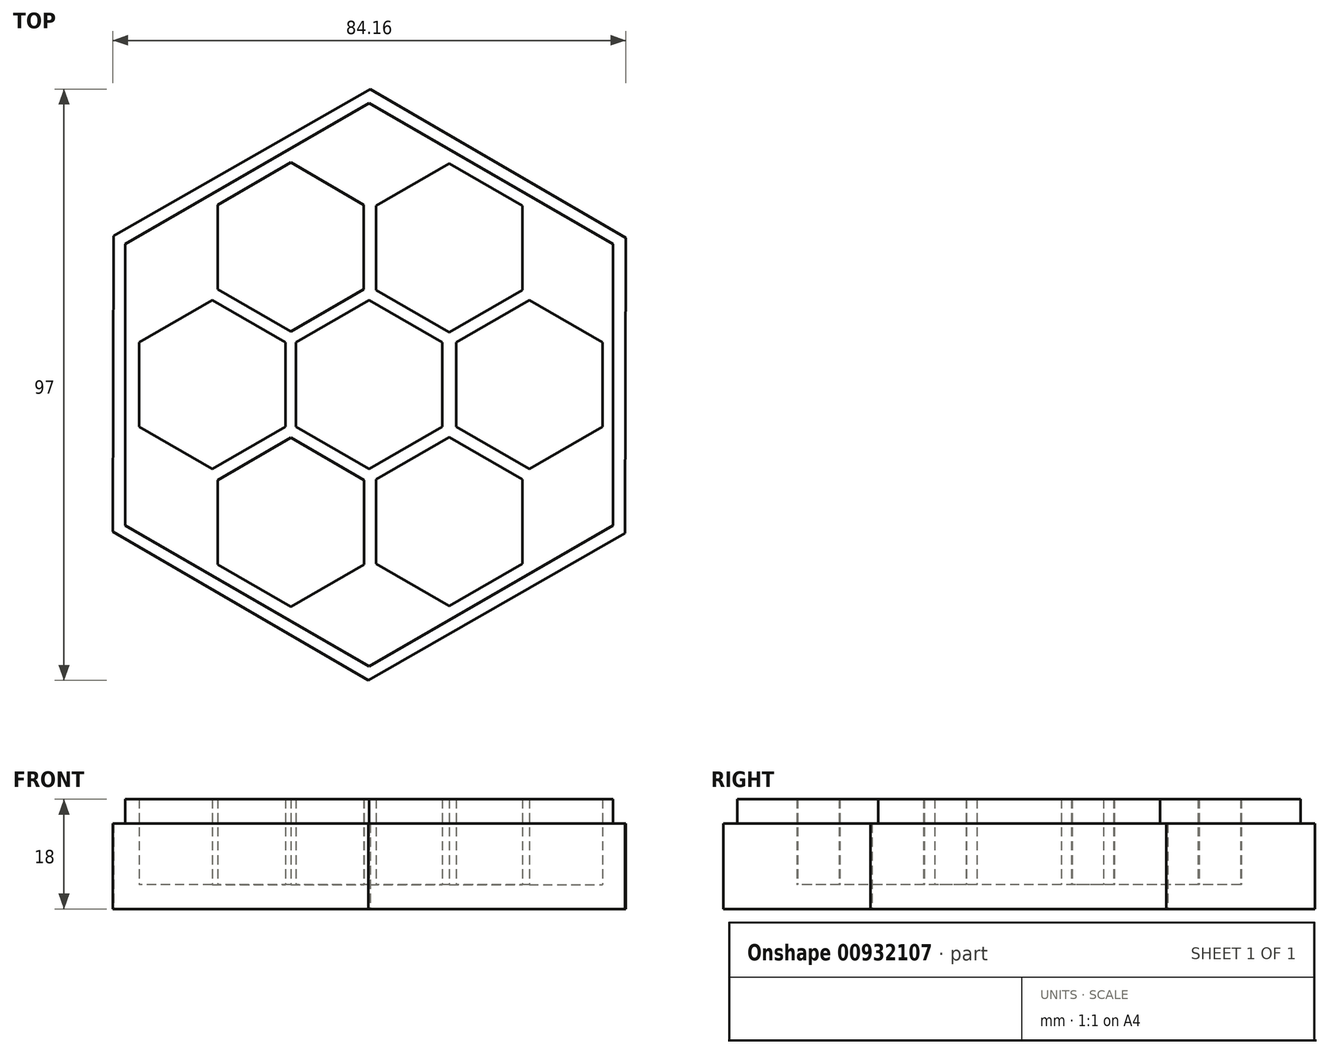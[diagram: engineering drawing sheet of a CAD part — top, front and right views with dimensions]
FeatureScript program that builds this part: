
annotation { "Feature Type Name" : "Feature", "Feature Type Description" : "" }
export const myFeature = defineFeature(function(context is Context, id is Id, definition is map)
    precondition{}
    {
        {
            var Q0;
            Q0=qCreatedBy(makeId("Top.planeOp"),FACE);
            var sketch = newSketch(context, id + "F0", { "sketchPlane" : qUnion([Q0])});
            skCircle(sketch, "E0.cCircle", {"center": v(0, 0) * mm, "radius": 12 * mm, "construction": true});
            skLineSegment(sketch, "E0.0", {"start": v(12, 6.93) * mm, "end": v(12, -6.93) * mm});
            skLineSegment(sketch, "E0.1", {"start": v(12, -6.93) * mm, "end": v(0, -13.86) * mm});
            skLineSegment(sketch, "E0.2", {"start": v(0, -13.86) * mm, "end": v(-12, -6.93) * mm});
            skLineSegment(sketch, "E0.3", {"start": v(-12, -6.93) * mm, "end": v(-12, 6.93) * mm});
            skLineSegment(sketch, "E0.4", {"start": v(-12, 6.93) * mm, "end": v(0, 13.86) * mm});
            skLineSegment(sketch, "E0.5", {"start": v(0, 13.86) * mm, "end": v(12, 6.93) * mm});
            skPoint(sketch, "E0.0.midPoint", {"position": v(12, 0) * mm});
            skCircle(sketch, "E1.cCircle", {"center": v(13.12, 22.45) * mm, "radius": 12 * mm, "construction": true});
            skLineSegment(sketch, "E1.0", {"start": v(25.12, 29.38) * mm, "end": v(25.12, 15.52) * mm});
            skLineSegment(sketch, "E1.1", {"start": v(25.12, 15.52) * mm, "end": v(13.12, 8.6) * mm});
            skLineSegment(sketch, "E1.2", {"start": v(13.12, 8.6) * mm, "end": v(1.12, 15.52) * mm});
            skLineSegment(sketch, "E1.3", {"start": v(1.12, 15.52) * mm, "end": v(1.12, 29.38) * mm});
            skLineSegment(sketch, "E1.4", {"start": v(1.12, 29.38) * mm, "end": v(13.12, 36.3) * mm});
            skLineSegment(sketch, "E1.5", {"start": v(13.12, 36.3) * mm, "end": v(25.12, 29.38) * mm});
            skPoint(sketch, "E1.0.midPoint", {"position": v(25.12, 22.45) * mm});
            skCircle(sketch, "E2.cCircle", {"center": v(-12.88, 22.58) * mm, "radius": 12 * mm, "construction": true});
            skLineSegment(sketch, "E2.0", {"start": v(-0.88, 29.51) * mm, "end": v(-0.88, 15.66) * mm});
            skLineSegment(sketch, "E2.1", {"start": v(-0.88, 15.66) * mm, "end": v(-12.88, 8.73) * mm});
            skLineSegment(sketch, "E2.2", {"start": v(-12.88, 8.73) * mm, "end": v(-24.88, 15.66) * mm});
            skLineSegment(sketch, "E2.3", {"start": v(-24.88, 15.66) * mm, "end": v(-24.88, 29.51) * mm});
            skLineSegment(sketch, "E2.4", {"start": v(-24.88, 29.51) * mm, "end": v(-12.88, 36.44) * mm});
            skLineSegment(sketch, "E2.5", {"start": v(-12.88, 36.44) * mm, "end": v(-0.88, 29.51) * mm});
            skPoint(sketch, "E2.0.midPoint", {"position": v(-0.88, 22.58) * mm});
            skCircle(sketch, "E3.cCircle", {"center": v(-25.77, 0) * mm, "radius": 12 * mm, "construction": true});
            skLineSegment(sketch, "E3.0", {"start": v(-13.77, 6.93) * mm, "end": v(-13.77, -6.93) * mm});
            skLineSegment(sketch, "E3.1", {"start": v(-13.77, -6.93) * mm, "end": v(-25.77, -13.86) * mm});
            skLineSegment(sketch, "E3.2", {"start": v(-25.77, -13.86) * mm, "end": v(-37.77, -6.93) * mm});
            skLineSegment(sketch, "E3.3", {"start": v(-37.77, -6.93) * mm, "end": v(-37.77, 6.93) * mm});
            skLineSegment(sketch, "E3.4", {"start": v(-37.77, 6.93) * mm, "end": v(-25.77, 13.86) * mm});
            skLineSegment(sketch, "E3.5", {"start": v(-25.77, 13.86) * mm, "end": v(-13.77, 6.93) * mm});
            skPoint(sketch, "E3.0.midPoint", {"position": v(-13.77, 0) * mm});
            skCircle(sketch, "E4.cCircle", {"center": v(13.14, -22.46) * mm, "radius": 12 * mm, "construction": true});
            skLineSegment(sketch, "E4.0", {"start": v(25.14, -15.54) * mm, "end": v(25.14, -29.4) * mm});
            skLineSegment(sketch, "E4.1", {"start": v(25.14, -29.4) * mm, "end": v(13.14, -36.32) * mm});
            skLineSegment(sketch, "E4.2", {"start": v(13.14, -36.32) * mm, "end": v(1.14, -29.4) * mm});
            skLineSegment(sketch, "E4.3", {"start": v(1.14, -29.4) * mm, "end": v(1.14, -15.54) * mm});
            skLineSegment(sketch, "E4.4", {"start": v(1.14, -15.54) * mm, "end": v(13.14, -8.6) * mm});
            skLineSegment(sketch, "E4.5", {"start": v(13.14, -8.6) * mm, "end": v(25.14, -15.54) * mm});
            skPoint(sketch, "E4.0.midPoint", {"position": v(25.14, -22.46) * mm});
            skCircle(sketch, "E5.cCircle", {"center": v(26.23, 0) * mm, "radius": 12 * mm, "construction": true});
            skLineSegment(sketch, "E5.0", {"start": v(38.23, 6.93) * mm, "end": v(38.23, -6.93) * mm});
            skLineSegment(sketch, "E5.1", {"start": v(38.23, -6.93) * mm, "end": v(26.23, -13.86) * mm});
            skLineSegment(sketch, "E5.2", {"start": v(26.23, -13.86) * mm, "end": v(14.23, -6.93) * mm});
            skLineSegment(sketch, "E5.3", {"start": v(14.23, -6.93) * mm, "end": v(14.23, 6.93) * mm});
            skLineSegment(sketch, "E5.4", {"start": v(14.23, 6.93) * mm, "end": v(26.23, 13.86) * mm});
            skLineSegment(sketch, "E5.5", {"start": v(26.23, 13.86) * mm, "end": v(38.23, 6.93) * mm});
            skPoint(sketch, "E5.0.midPoint", {"position": v(38.23, 0) * mm});
            skCircle(sketch, "E6.cCircle", {"center": v(-12.86, -22.57) * mm, "radius": 12 * mm, "construction": true});
            skLineSegment(sketch, "E6.0", {"start": v(-0.86, -15.64) * mm, "end": v(-0.86, -29.5) * mm});
            skLineSegment(sketch, "E6.1", {"start": v(-0.86, -29.5) * mm, "end": v(-12.86, -36.43) * mm});
            skLineSegment(sketch, "E6.2", {"start": v(-12.86, -36.43) * mm, "end": v(-24.86, -29.5) * mm});
            skLineSegment(sketch, "E6.3", {"start": v(-24.86, -29.5) * mm, "end": v(-24.86, -15.64) * mm});
            skLineSegment(sketch, "E6.4", {"start": v(-24.86, -15.64) * mm, "end": v(-12.86, -8.71) * mm});
            skLineSegment(sketch, "E6.5", {"start": v(-12.86, -8.71) * mm, "end": v(-0.86, -15.64) * mm});
            skPoint(sketch, "E6.0.midPoint", {"position": v(-0.86, -22.57) * mm});
            skCircle(sketch, "E7.cCircle", {"center": v(0, 0) * mm, "radius": 42 * mm, "construction": true});
            skLineSegment(sketch, "E7.0", {"start": v(0.16, 48.5) * mm, "end": v(42.08, 24.11) * mm});
            skLineSegment(sketch, "E7.1", {"start": v(42.08, 24.11) * mm, "end": v(41.92, -24.38) * mm});
            skLineSegment(sketch, "E7.2", {"start": v(41.92, -24.38) * mm, "end": v(-0.16, -48.5) * mm});
            skLineSegment(sketch, "E7.3", {"start": v(-0.16, -48.5) * mm, "end": v(-42.08, -24.11) * mm});
            skLineSegment(sketch, "E7.4", {"start": v(-42.08, -24.11) * mm, "end": v(-41.92, 24.38) * mm});
            skLineSegment(sketch, "E7.5", {"start": v(-41.92, 24.38) * mm, "end": v(0.16, 48.5) * mm});
            skPoint(sketch, "E7.0.midPoint", {"position": v(21.12, 36.3) * mm});
            skCircle(sketch, "E8.cCircle", {"center": v(0, 0) * mm, "radius": 40 * mm, "construction": true});
            skLineSegment(sketch, "E8.0", {"start": v(0, 46.19) * mm, "end": v(40, 23.1) * mm});
            skLineSegment(sketch, "E8.1", {"start": v(40, 23.1) * mm, "end": v(40, -23.1) * mm});
            skLineSegment(sketch, "E8.2", {"start": v(40, -23.1) * mm, "end": v(0, -46.19) * mm});
            skLineSegment(sketch, "E8.3", {"start": v(0, -46.19) * mm, "end": v(-40, -23.1) * mm});
            skLineSegment(sketch, "E8.4", {"start": v(-40, -23.1) * mm, "end": v(-40, 23.1) * mm});
            skLineSegment(sketch, "E8.5", {"start": v(-40, 23.1) * mm, "end": v(0, 46.19) * mm});
            skPoint(sketch, "E8.0.midPoint", {"position": v(20, 34.64) * mm});
            skSolve(sketch);
        }
        {
            var Q0;
            Q0 = qSketchRegion(id + "F0", true);
            extrude(context, id + "F1", {"entities" : qUnion([Q0]), "depth" : 14 * mm, "offsetDistance" : 25.4 * mm});
        }
        {
            var Q0;
            Q0=makeQuery(id+"F0.imprint","IMPRINT",FACE,{"disambiguationData":[TD([[makeQuery(id+"F0.imprint","IMPRINT",EDGE,{"derivedFrom":sQuery(id+"F0.wireOp",EDGE,"E0.0")}),1.0]])]});
            extrude(context, id + "F2", {"entities" : qUnion([Q0]), "operationType" : NewBodyOperationType.ADD, "depth" : 18 * mm, "offsetDistance" : 25.4 * mm});
        }
        {
            var Q0;
            Q0=makeQuery(id+"F0.imprint","IMPRINT",FACE,{"disambiguationData":[TD([[makeQuery(id+"F0.imprint","IMPRINT",EDGE,{"derivedFrom":sQuery(id+"F0.wireOp",EDGE,"E1.0")}),-1.0]])]});
            var Q1;
            Q1=makeQuery(id+"F0.imprint","IMPRINT",FACE,{"disambiguationData":[TD([[makeQuery(id+"F0.imprint","IMPRINT",EDGE,{"derivedFrom":sQuery(id+"F0.wireOp",EDGE,"E2.0")}),-1.0]])]});
            var Q2;
            Q2=makeQuery(id+"F0.imprint","IMPRINT",FACE,{"disambiguationData":[TD([[makeQuery(id+"F0.imprint","IMPRINT",EDGE,{"derivedFrom":sQuery(id+"F0.wireOp",EDGE,"E3.0")}),-1.0]])]});
            var Q3;
            Q3=makeQuery(id+"F0.imprint","IMPRINT",FACE,{"disambiguationData":[TD([[makeQuery(id+"F0.imprint","IMPRINT",EDGE,{"derivedFrom":sQuery(id+"F0.wireOp",EDGE,"E0.0")}),-1.0]])]});
            var Q4;
            Q4=makeQuery(id+"F0.imprint","IMPRINT",FACE,{"disambiguationData":[TD([[makeQuery(id+"F0.imprint","IMPRINT",EDGE,{"derivedFrom":sQuery(id+"F0.wireOp",EDGE,"E5.0")}),-1.0]])]});
            var Q5;
            Q5=makeQuery(id+"F0.imprint","IMPRINT",FACE,{"disambiguationData":[TD([[makeQuery(id+"F0.imprint","IMPRINT",EDGE,{"derivedFrom":sQuery(id+"F0.wireOp",EDGE,"E4.0")}),-1.0]])]});
            var Q6;
            Q6=makeQuery(id+"F0.imprint","IMPRINT",FACE,{"disambiguationData":[TD([[makeQuery(id+"F0.imprint","IMPRINT",EDGE,{"derivedFrom":sQuery(id+"F0.wireOp",EDGE,"E6.0")}),-1.0]])]});
            extrude(context, id + "F3", {"entities" : qUnion([Q0, Q1, Q2, Q3, Q4, Q5, Q6]), "operationType" : NewBodyOperationType.ADD, "depth" : 4 * mm, "offsetDistance" : 25.4 * mm});
        }
    });
